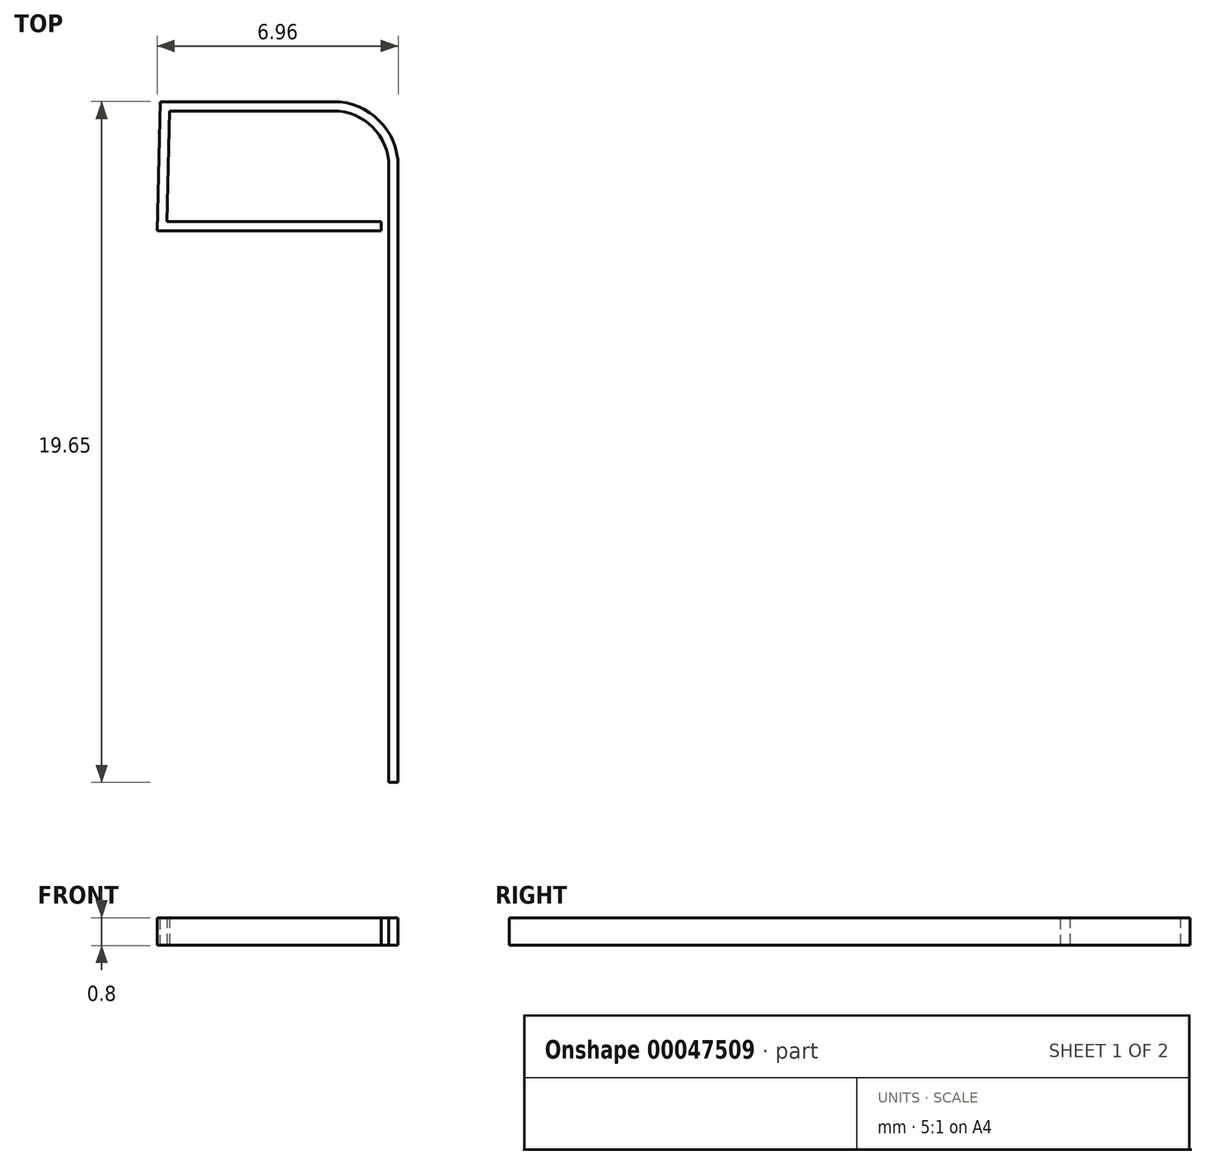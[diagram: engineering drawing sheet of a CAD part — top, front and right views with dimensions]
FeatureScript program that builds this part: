
annotation { "Feature Type Name" : "Feature", "Feature Type Description" : "" }
export const myFeature = defineFeature(function(context is Context, id is Id, definition is map)
    precondition{}
    {
        {
            var Q0;
            Q0=qCreatedBy(makeId("Top.planeOp"),FACE);
            var sketch = newSketch(context, id + "F0", { "sketchPlane" : qUnion([Q0])});
            skArc(sketch, "E0", {"start": v(1.59, 0) * mm, "mid": v(1.12, 1.12) * mm, "end": v(0, 1.59) * mm});
            skPoint(sketch, "E1.start.orphan", {"position": v(0, 2.42) * mm});
            skLineSegment(sketch, "E2", {"start": v(1.59, 0) * mm, "end": v(1.59, -17.78) * mm});
            skLineSegment(sketch, "E3", {"start": v(0, -1.59) * mm, "end": v(1.38, -1.59) * mm});
            skPoint(sketch, "E4", {"position": v(1.38, -1.59) * mm});
            skLineSegment(sketch, "E5", {"start": v(0, 1.59) * mm, "end": v(-4.72, 1.59) * mm});
            skLineSegment(sketch, "E6", {"start": v(0, -1.59) * mm, "end": v(-4.8, -1.59) * mm});
            skLineSegment(sketch, "E7", {"start": v(-4.8, -1.59) * mm, "end": v(-4.72, 1.59) * mm});
            skSolve(sketch);
        }
        {
            var Q0;
            Q0=sQuery(id+"F0.wireOp",VERTEX,"E2.end");
            var Q1;
            Q1=qCreatedBy(makeId("Front.planeOp"),FACE);
            cPlane(context, id + "F1", {"entities" : qUnion([Q0, Q1]), "cplaneType" : CPlaneType.PLANE_POINT, "offset" : 152.4 * mm, "width" : 152.4 * mm, "height" : 152.4 * mm});
        }
        {
            var Q0;
            Q0=qCreatedBy(id+"F1.planeOp",FACE);
            var sketch = newSketch(context, id + "F2", { "sketchPlane" : qUnion([Q0])});
            skLineSegment(sketch, "E8.rect.bottom", {"start": v(1.87, -0.4) * mm, "end": v(1.6, -0.4) * mm});
            skLineSegment(sketch, "E8.rect.top", {"start": v(1.87, 0.4) * mm, "end": v(1.6, 0.4) * mm});
            skLineSegment(sketch, "E8.rect.left", {"start": v(1.87, -0.4) * mm, "end": v(1.87, 0.4) * mm});
            skPoint(sketch, "E8.rect.middle", {"position": v(1.6, 0) * mm});
            skLineSegment(sketch, "E9", {"start": v(1.6, -0.4) * mm, "end": v(1.6, 0.4) * mm});
            skPoint(sketch, "E8.rect.right.start.orphan", {"position": v(1.33, -0.4) * mm});
            skPoint(sketch, "E10.orphan", {"position": v(1.33, 0.4) * mm});
            skSolve(sketch);
        }
        {
            var Q0;
            Q0=makeQuery(id+"F2.imprint","IMPRINT",FACE,{"disambiguationData":[TD([[makeQuery(id+"F2.imprint","IMPRINT",EDGE,{"derivedFrom":sQuery(id+"F2.wireOp",EDGE,"E8.rect.bottom")}),-1.0]])]});
            var Q1;
            Q1 = qConstructionFilter(qBodyType(qCreatedBy(id + "F0" ,EDGE), BodyType.WIRE), ConstructionObject.NO);
            sweep(context, id + "F3", {"profiles" : qUnion([Q0]), "path" : qUnion([Q1])});
        }
    });
